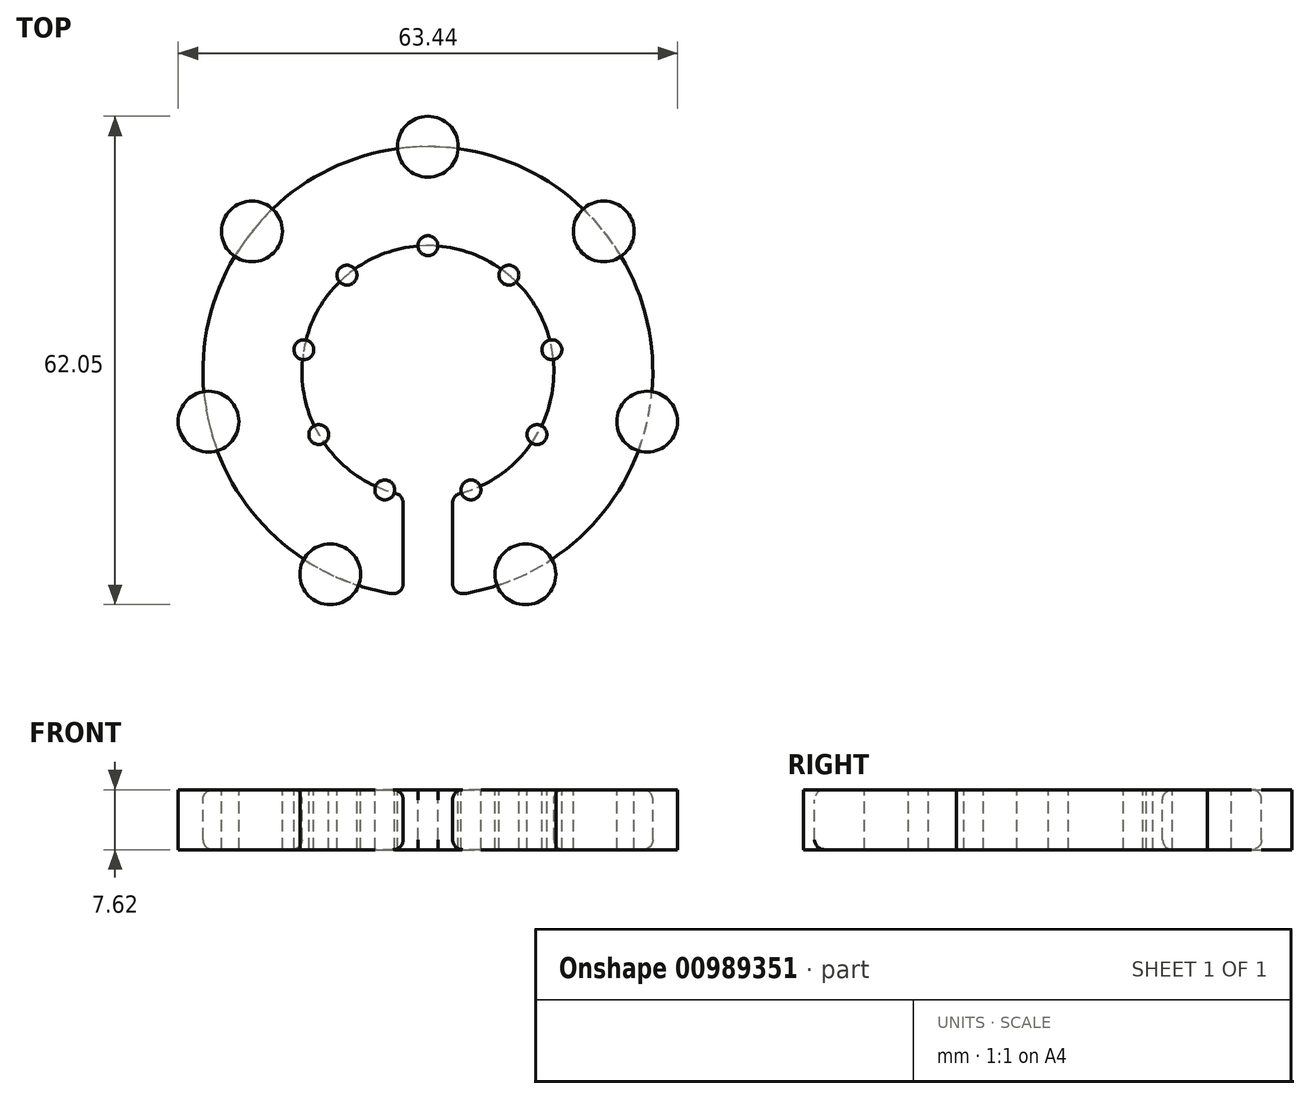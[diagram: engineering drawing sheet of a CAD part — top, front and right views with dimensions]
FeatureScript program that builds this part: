
annotation { "Feature Type Name" : "Feature", "Feature Type Description" : "" }
export const myFeature = defineFeature(function(context is Context, id is Id, definition is map)
    precondition{}
    {
        {
            var Q0;
            Q0=qCreatedBy(makeId("Top.planeOp"),FACE);
            var sketch = newSketch(context, id + "F0", { "sketchPlane" : qUnion([Q0])});
            skCircle(sketch, "E0", {"center": v(0, 0) * mm, "radius": 28.57 * mm});
            skCircle(sketch, "E1", {"center": v(0, 0) * mm, "radius": 14.75 * mm, "construction": true});
            skCircle(sketch, "E2", {"center": v(0, 0) * mm, "radius": 16 * mm});
            skSolve(sketch);
        }
        {
            var Q0;
            Q0=makeQuery(id+"F0.imprint","IMPRINT",FACE,{"disambiguationData":[TD([[makeQuery(id+"F0.imprint","IMPRINT",EDGE,{"derivedFrom":sQuery(id+"F0.wireOp",EDGE,"E0")}),1.0]])]});
            extrude(context, id + "F1", {"entities" : qUnion([Q0]), "oppositeDirection" : true, "depth" : 7.62 * mm, "offsetDistance" : 25.4 * mm});
        }
        {
            var Q0;
            Q0=makeQuery(id+"F1.opExtrude","CAP_FACE",FACE,{"disambiguationData":[OSD([sQuery(id+"F0.wireOp",EDGE,"E0"),sQuery(id+"F0.wireOp",EDGE,"E2")])],"isStart":true});
            var sketch = newSketch(context, id + "F2", { "sketchPlane" : qUnion([Q0])});
            skCircle(sketch, "E3", {"center": v(0, 16) * mm, "radius": 1.26 * mm});
            skCircle(sketch, "E4", {"center": v(0, 28.57) * mm, "radius": 3.86 * mm});
            skSolve(sketch);
        }
        {
            var Q0;
            Q0 = qSketchRegion(id + "F2", true);
            extrude(context, id + "F3", {"entities" : qUnion([Q0]), "oppositeDirection" : true, "depth" : 7.62 * mm, "offsetDistance" : 25.4 * mm});
        }
        {
            var Q0;
            Q0=makeQuery(id+"F3.opExtrude","SWEPT_BODY",BODY,{"disambiguationData":[OSD([sQuery(id+"F2.wireOp",EDGE,"E4")])]});
            var Q1;
            Q1=sQuery(id+"F0.wireOp",EDGE,"E0");
            circularPattern(context, id + "F4", {"entities" : qUnion([Q0]), "axis" : qUnion([Q1]), "angle" : 360 * degree, "instanceCount" : 7, "equalSpace" : true});
        }
        {
            var Q0;
            Q0=makeQuery(id+"F3.opExtrude","SWEPT_BODY",BODY,{"disambiguationData":[OSD([sQuery(id+"F2.wireOp",EDGE,"E3")])]});
            var Q1;
            Q1=sQuery(id+"F0.wireOp",EDGE,"E2");
            circularPattern(context, id + "F5", {"entities" : qUnion([Q0]), "axis" : qUnion([Q1]), "angle" : 360 * degree, "instanceCount" : 9, "equalSpace" : true});
        }
        {
            var Q0;
            Q0=makeQuery(id+"F1.opExtrude","CAP_FACE",FACE,{"disambiguationData":[OSD([sQuery(id+"F0.wireOp",EDGE,"E0"),sQuery(id+"F0.wireOp",EDGE,"E2")])],"isStart":false});
            var sketch = newSketch(context, id + "F6", { "sketchPlane" : qUnion([Q0])});
            skLineSegment(sketch, "E5.bottom", {"start": v(3.14, 32.24) * mm, "end": v(-3.14, 32.24) * mm});
            skLineSegment(sketch, "E5.top", {"start": v(3.14, 13.19) * mm, "end": v(-3.14, 13.19) * mm});
            skLineSegment(sketch, "E5.left", {"start": v(3.14, 32.24) * mm, "end": v(3.14, 13.19) * mm});
            skLineSegment(sketch, "E5.right", {"start": v(-3.14, 32.24) * mm, "end": v(-3.14, 13.19) * mm});
            skPoint(sketch, "E5.middle", {"position": v(0, 22.71) * mm});
            skSolve(sketch);
        }
        {
            var Q0;
            {var subQ0=sQuery(id+"F6.wireOp",EDGE,"E5.left");var subQ1=makeQuery(id+"F1.opExtrude","CAP_EDGE",EDGE,{"disambiguationData":[OSD([sQuery(id+"F0.wireOp",EDGE,"E0")])],"isStart":false});var subQ2=makeQuery(id+"F6.imprint","INTERSECT",VERTEX,{"derivedFrom":[subQ1,subQ0]});Q0=makeQuery(id+"F6.imprint","IMPRINT",FACE,{"disambiguationData":[TD([[makeQuery(id+"F6.imprint","IMPRINT",EDGE,{"disambiguationData":[TD([[subQ2,-1.0]])],"derivedFrom":subQ0}),-1.0]])]});}
            extrude(context, id + "F7", {"entities" : qUnion([Q0]), "operationType" : NewBodyOperationType.REMOVE, "oppositeDirection" : true, "depth" : 25.4 * mm, "offsetDistance" : 25.4 * mm});
        }
        {
            var Q0;
            Q0=makeQuery(id+"F1.opExtrude","CAP_FACE",FACE,{"disambiguationData":[OSD([sQuery(id+"F0.wireOp",EDGE,"E0"),sQuery(id+"F0.wireOp",EDGE,"E2")])],"isStart":false});
            var Q1;
            Q1=makeQuery(id+"F1.opExtrude","CAP_FACE",FACE,{"disambiguationData":[OSD([sQuery(id+"F0.wireOp",EDGE,"E0"),sQuery(id+"F0.wireOp",EDGE,"E2")])],"isStart":true});
            var Q2;
            Q2=makeQuery(id+"F7.boolean.opBoolean","COPY",FACE,{"derivedFrom":makeQuery(id+"F7.opExtrude","SWEPT_FACE",FACE,{"disambiguationData":[OSD([sQuery(id+"F6.wireOp",EDGE,"E5.left")])]})});
            var Q3;
            Q3=makeQuery(id+"F7.boolean.opBoolean","COPY",FACE,{"derivedFrom":makeQuery(id+"F7.opExtrude","SWEPT_FACE",FACE,{"disambiguationData":[OSD([sQuery(id+"F6.wireOp",EDGE,"E5.right")])]})});
            fillet(context, id + "F8", {"entities" : qUnion([Q0, Q1, Q2, Q3]), "radius" : 1.27 * mm, "tangentPropagation" : true, "allowEdgeOverflow" : false});
        }
    });
